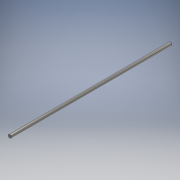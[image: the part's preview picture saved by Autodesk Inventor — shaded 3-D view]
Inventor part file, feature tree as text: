
AUTODESK INVENTOR PART (.ipt)
format: ipt  version: 2017.1 (Build 211199000, 199)  size: 95,744 bytes
history: native  units: mm
features: extrude x1, chamfer x1, sketch x1
ambient origin geometry x8: Origin, YZ Plane, XZ Plane, XY Plane, X Axis, Y Axis, Z Axis, Center Point
bodies: Solid1 (feature_tree)
feature tree (3):
  extrude  "Extrusion1"  Depth=500.0mm TaperAngle=0.0deg
  chamfer  "Chamfer1"  Distance=0.5mm Angle=45.0deg
  sketch  "Sketch1"  dims[d0=10.0mm d1=500.0mm d2=0.0mm d3=0.5mm d4=2.0mm d5=45.0deg]
